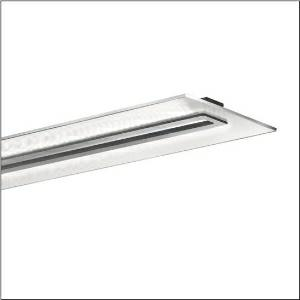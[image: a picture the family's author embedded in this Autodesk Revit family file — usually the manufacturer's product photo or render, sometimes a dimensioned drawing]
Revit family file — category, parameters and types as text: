
# Revit family: vega_r__11_5mn238dle0s_e1af
name_source: partatom
category: Lighting Fixtures
units: mm (PartAtom-declared; Revit-internal decimal feet)

## family parameters
Cut with Voids When Loaded = No
Host = Face
Light Source = No
Part Type = Normal
Room Calculation Point = No
Round Connector Dimension = Use Diameter
Shared = No

## types (1)
- --- (1 x LED 4000K / CRI = 80 (unbekannt), 8130 lm, 4000K)
    Apparent Load = 62 VA
    CIE Flux Codes = 61 86 97 62 100
    Color Rendering = 80
    Color Temperature = 4000K
    Default Elevation = 1800 mm
    Description = Vega® 11, office luminaire, primary light control with prismatic reflector, of PMMA, transparent prismatic structure, CAT 2 (L<= 1500cd/m²), light emission: direct/indirect distribution, primary light characteristic: symmetric, installation type: suspended mounting, surface-mounted, LED, rated luminous flux: 8.130lm, luminous efficacy: 131lm/W, light colour: 840, colour temperature: 4000K, control gear: DALI, with terminal, 3+2-pole, max. 2.5mm², mains connection: 230V, AC, 50Hz, connection cable inclusive, cable length: 1,5m, rated input power: 62W, luminaire housing, rectangular, rounded, of aluminium section, anodised, metallic grey (RAL 9006), length: 1.250mm, width: 350mm, height: 43mm, luminaire housing, lower part, of aluminium section, anodised, metallic grey (RAL 9006), of PC, grey, protection rating (complete): IP20, insulation class (complete): insulation class I (protective earthing), certification: CE, permissible operating ambient temperature: 0..+35°C, standard: EN 50419, packaging unit: 1 piece
    Height = 40 mm  [stored 0.131234 ft]
    Lamp = 1 x LED 4000K / CRI >= 80 (unbekannt)
    Lamp Light Flux = 8130 lm
    Lamp count = 1
    Length = 1250 mm
    Luminous efficacy = 131 lm/W
    Manufacturer = Siteco
    ModVariant = No
    Model = 5MN238DLE0S
    Mounting Place = Ceiling
    Mounting Type = Pendant
    Number of Poles = 1
    OnlyDefault = Yes
    Power Factor = 1
    Product Name = Vega® 11
    Product group = office luminaire | ceiling pendant
    ProductGroupID = 903
    Protection Class = Protection class I
    Protection Degree = IP 20
    RLX_Detail_Level = 1
    RLX_Emergency_Light_Flux = 0 lm
    RLX_Emergency_Type = 0
    RLX_Emergency_Type_DB = No
    RlxData = <blob elided: 63013 chars, md5=0ee7bd28>
    Socket = socket
    Standby Power = 0 W
    System Light Flux = 8130 lm
    System Power = 62 W
    Type Comments = factory setting: luminous flux: 100 % | dim-lin: 254 | 458 mA
    Type Image = l_1004807.jpg
    URL = http://relux.com
    VarID = @adj_220921
    Voltage = 0 V
    Weight = 0.00 kg
    Width = 350 mm

note: [stored X ft] marks values corroborated as IEEE doubles in the binary element streams (Revit-internal decimal feet)

## geometry (parser evidence)
native form markers: Blend x4, Sweep x14
no freeform markers — native parametric forms only
